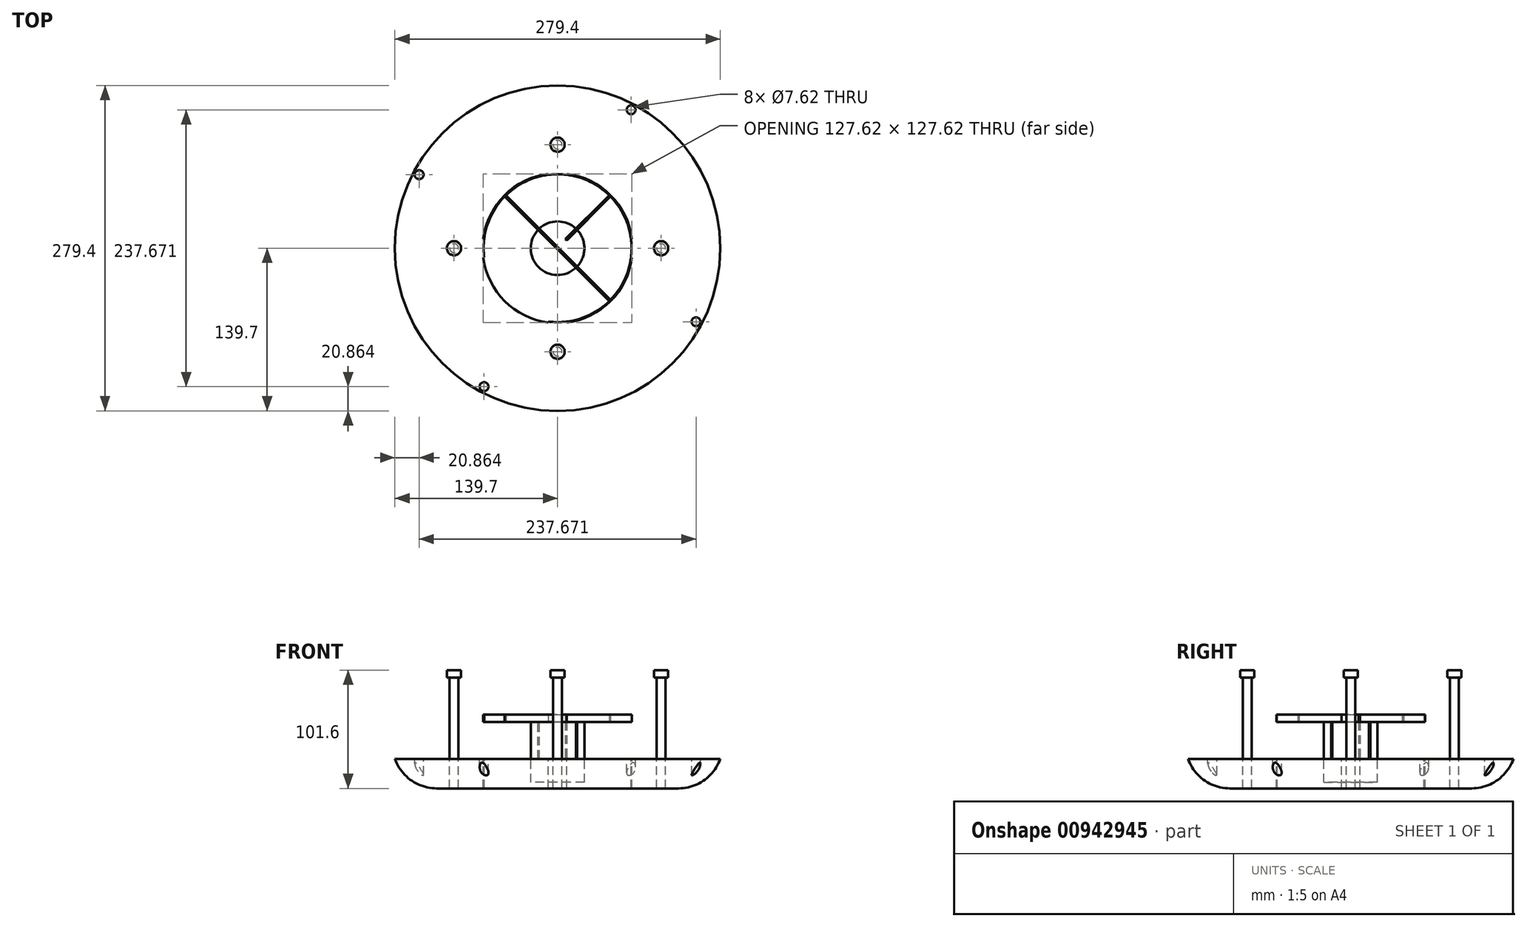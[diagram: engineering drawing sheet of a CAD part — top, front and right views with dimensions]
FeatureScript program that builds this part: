
annotation { "Feature Type Name" : "Feature", "Feature Type Description" : "" }
export const myFeature = defineFeature(function(context is Context, id is Id, definition is map)
    precondition{}
    {
        {
            var Q0;
            Q0=qCreatedBy(makeId("Top.planeOp"),FACE);
            var sketch = newSketch(context, id + "F0", { "sketchPlane" : qUnion([Q0])});
            skArc(sketch, "E0", {"start": v(-7.87, 63.01) * mm, "mid": v(-44.9, 44.9) * mm, "end": v(-63.01, 7.87) * mm});
            skArc(sketch, "E1", {"start": v(-7.87, 63.81) * mm, "mid": v(-45.46, 45.46) * mm, "end": v(-63.81, 7.87) * mm});
            skLineSegment(sketch, "E2", {"start": v(-7.87, 63.81) * mm, "end": v(-7.87, 63.01) * mm});
            skLineSegment(sketch, "E3", {"start": v(7.87, 63.01) * mm, "end": v(7.87, 63.81) * mm});
            skLineSegment(sketch, "E4.MirrorCS", {"start": v(-7.87, -63.81) * mm, "end": v(-7.87, -63.01) * mm});
            skLineSegment(sketch, "E5", {"start": v(-63.81, 7.87) * mm, "end": v(-63.01, 7.87) * mm});
            skLineSegment(sketch, "E6", {"start": v(-63.01, 7.87) * mm, "end": v(-63.81, 7.87) * mm});
            skLineSegment(sketch, "E7", {"start": v(63.01, 7.87) * mm, "end": v(63.81, 7.87) * mm});
            skLineSegment(sketch, "E8.MirrorCS", {"start": v(-63.81, -7.87) * mm, "end": v(-63.01, -7.87) * mm});
            skLineSegment(sketch, "E9.MirrorCS", {"start": v(63.01, -7.87) * mm, "end": v(63.81, -7.87) * mm});
            skLineSegment(sketch, "E10.MirrorCS", {"start": v(-63.01, -7.87) * mm, "end": v(-63.81, -7.87) * mm});
            skArc(sketch, "E11.trimOffspring", {"start": v(-63.81, -7.87) * mm, "mid": v(-45.46, -45.46) * mm, "end": v(-7.87, -63.81) * mm});
            skArc(sketch, "E12.trimOffspring", {"start": v(-63.01, -7.87) * mm, "mid": v(-44.9, -44.9) * mm, "end": v(-7.87, -63.01) * mm});
            skArc(sketch, "E13.trimOffspring", {"start": v(63.81, 7.87) * mm, "mid": v(45.46, 45.46) * mm, "end": v(7.87, 63.81) * mm});
            skArc(sketch, "E14.trimOffspring", {"start": v(63.01, 7.87) * mm, "mid": v(44.9, 44.9) * mm, "end": v(7.87, 63.01) * mm});
            skArc(sketch, "E15.trimOffspring", {"start": v(7.87, -63.01) * mm, "mid": v(44.9, -44.9) * mm, "end": v(63.01, -7.87) * mm});
            skArc(sketch, "E16.trimOffspring", {"start": v(7.87, -63.81) * mm, "mid": v(45.46, -45.46) * mm, "end": v(63.81, -7.87) * mm});
            skLineSegment(sketch, "E17", {"start": v(-9, 7.87) * mm, "end": v(44.34, -45.46) * mm});
            skLineSegment(sketch, "E18.MirrorCS", {"start": v(45.46, -44.34) * mm, "end": v(-44.34, 45.46) * mm});
            skLineSegment(sketch, "E19", {"start": v(44.34, -45.46) * mm, "end": v(-45.46, 44.34) * mm});
            skLineSegment(sketch, "E20", {"start": v(-7.87, -6.75) * mm, "end": v(-45.46, -44.34) * mm});
            skLineSegment(sketch, "E21", {"start": v(-45.46, -44.34) * mm, "end": v(-7.87, -6.75) * mm});
            skLineSegment(sketch, "E22.MirrorCS", {"start": v(-44.34, -45.46) * mm, "end": v(-6.75, -7.87) * mm});
            skLineSegment(sketch, "E23.trimOffspring", {"start": v(-7.87, 63.01) * mm, "end": v(-7.87, 63.81) * mm});
            skLineSegment(sketch, "E24.trimOffspring", {"start": v(-7.87, -63.01) * mm, "end": v(-7.87, -63.81) * mm});
            skLineSegment(sketch, "E25.trimOffspring", {"start": v(7.87, -63.01) * mm, "end": v(7.87, -63.81) * mm});
            skLineSegment(sketch, "E26.trimOffspring", {"start": v(6.75, 7.87) * mm, "end": v(44.34, 45.46) * mm});
            skLineSegment(sketch, "E27.trimOffspring", {"start": v(7.87, 6.75) * mm, "end": v(45.46, 44.34) * mm});
            skCircle(sketch, "E28", {"center": v(0, 0) * mm, "radius": 63.5 * mm});
            skCircle(sketch, "E29", {"center": v(0, 0) * mm, "radius": 139.7 * mm});
            skCircle(sketch, "E30", {"center": v(0, 0) * mm, "radius": 95.25 * mm});
            skLineSegment(sketch, "E31", {"start": v(-7.87, -6.75) * mm, "end": v(-6.75, -7.87) * mm});
            skLineSegment(sketch, "E32", {"start": v(6.75, 7.87) * mm, "end": v(7.87, 6.75) * mm});
            skPoint(sketch, "E33.orphan", {"position": v(-7.87, 7.87) * mm});
            skPoint(sketch, "E34.MirrorCS.start.orphan", {"position": v(-7.87, 0) * mm});
            skPoint(sketch, "E35.MirrorCS.start.orphan", {"position": v(7.87, 0) * mm});
            skLineSegment(sketch, "E36", {"start": v(-7.3, -7.3) * mm, "end": v(0, 0) * mm});
            skLineSegment(sketch, "E37", {"start": v(0, 63.5) * mm, "end": v(0, 88.9) * mm});
            skCircle(sketch, "E38", {"center": v(0, 88.9) * mm, "radius": 3.81 * mm});
            skCircle(sketch, "E39.MirrorC", {"center": v(0, -88.9) * mm, "radius": 3.81 * mm});
            skCircle(sketch, "E40.1.0", {"center": v(-88.9, 0) * mm, "radius": 3.81 * mm});
            skCircle(sketch, "E40.3.0", {"center": v(88.9, 0) * mm, "radius": 3.81 * mm});
            skLineSegment(sketch, "E41", {"start": v(68.85, 121.56) * mm, "end": v(63.11, 118.84) * mm});
            skCircle(sketch, "E42", {"center": v(63.11, 118.84) * mm, "radius": 3.81 * mm});
            skCircle(sketch, "E43.1.0", {"center": v(-118.84, 63.11) * mm, "radius": 3.81 * mm});
            skCircle(sketch, "E43.2.0", {"center": v(-63.11, -118.84) * mm, "radius": 3.81 * mm});
            skCircle(sketch, "E43.3.0", {"center": v(118.84, -63.11) * mm, "radius": 3.81 * mm});
            skSolve(sketch);
        }
        {
            var Q0;
            {var subQ4=sQuery(id+"F0.wireOp",EDGE,"E1");Q0=makeQuery(id+"F0.imprint","IMPRINT",FACE,{"disambiguationData":[TD([[makeQuery(id+"F0.imprint","IMPRINT",EDGE,{"derivedFrom":subQ4}),1.0]])]});}
            var Q1;
            {var subQ1=sQuery(id+"F0.wireOp",EDGE,"E10.MirrorCS");Q1=makeQuery(id+"F0.imprint","IMPRINT",FACE,{"disambiguationData":[TD([[makeQuery(id+"F0.imprint","IMPRINT",EDGE,{"derivedFrom":subQ1}),1.0]])]});}
            var Q2;
            {var subQ4=sQuery(id+"F0.wireOp",EDGE,"E13.trimOffspring");Q2=makeQuery(id+"F0.imprint","IMPRINT",FACE,{"disambiguationData":[TD([[makeQuery(id+"F0.imprint","IMPRINT",EDGE,{"derivedFrom":subQ4}),1.0]])]});}
            var Q3;
            {var subQ1=sQuery(id+"F0.wireOp",EDGE,"E16.trimOffspring");Q3=makeQuery(id+"F0.imprint","IMPRINT",FACE,{"disambiguationData":[TD([[makeQuery(id+"F0.imprint","IMPRINT",EDGE,{"derivedFrom":subQ1}),1.0]])]});}
            var Q4;
            {var subQ4=sQuery(id+"F0.wireOp",EDGE,"E28");var subQ6=sQuery(id+"F0.wireOp",EDGE,"E18.MirrorCS");var subQ7=makeQuery(id+"F0.imprint","INTERSECT",VERTEX,{"disambiguationData":[OD(0.0)],"derivedFrom":[subQ6,subQ4]});Q4=makeQuery(id+"F0.imprint","IMPRINT",FACE,{"disambiguationData":[TD([[makeQuery(id+"F0.imprint","IMPRINT",EDGE,{"disambiguationData":[TD([[subQ7,-1.0]])],"derivedFrom":subQ6}),1.0]])]});}
            var Q5;
            {var subQ0=sQuery(id+"F0.wireOp",EDGE,"E21");var subQ8=makeQuery(id+"F0.imprint","INTERSECT",VERTEX,{"derivedFrom":[sQuery(id+"F0.wireOp",EDGE,"E8.MirrorCS"),subQ0]});Q5=makeQuery(id+"F0.imprint","IMPRINT",FACE,{"disambiguationData":[TD([[makeQuery(id+"F0.imprint","IMPRINT",EDGE,{"disambiguationData":[TD([[subQ8,1.0]])],"derivedFrom":subQ0}),-1.0]])]});}
            var Q6;
            {var subQ4=sQuery(id+"F0.wireOp",EDGE,"E32");Q6=makeQuery(id+"F0.imprint","IMPRINT",FACE,{"disambiguationData":[TD([[makeQuery(id+"F0.imprint","IMPRINT",EDGE,{"derivedFrom":subQ4}),1.0]])]});}
            extrude(context, id + "F1", {"entities" : qUnion([Q0, Q1, Q2, Q3, Q4, Q5, Q6]), "depth" : 38.1 * mm, "offsetDistance" : 25.4 * mm});
        }
        {
            var Q0;
            {var subQ10=sQuery(id+"F0.wireOp",EDGE,"E1");Q0=makeQuery(id+"F0.imprint","IMPRINT",FACE,{"disambiguationData":[TD([[makeQuery(id+"F0.imprint","IMPRINT",EDGE,{"derivedFrom":subQ10}),-1.0]])]});}
            extrude(context, id + "F2", {"entities" : qUnion([Q0]), "oppositeDirection" : true, "depth" : 25.4 * mm, "offsetDistance" : 25.4 * mm});
        }
        {
            var Q0;
            Q0=makeQuery(id+"F0.imprint","IMPRINT",FACE,{"disambiguationData":[TD([[makeQuery(id+"F0.imprint","IMPRINT",EDGE,{"derivedFrom":sQuery(id+"F0.wireOp",EDGE,"E29")}),1.0]])]});
            extrude(context, id + "F3", {"entities" : qUnion([Q0]), "operationType" : NewBodyOperationType.ADD, "oppositeDirection" : true, "depth" : 25.4 * mm, "offsetDistance" : 25.4 * mm});
        }
        {
            var Q0;
            Q0=makeQuery(id+"F3.opExtrude","CAP_EDGE",EDGE,{"disambiguationData":[OSD([sQuery(id+"F0.wireOp",EDGE,"E29")])],"isStart":false});
            fillet(context, id + "F4", {"entities" : qUnion([Q0]), "radius" : 38.1 * mm, "tangentPropagation" : true, "allowEdgeOverflow" : false});
        }
        {
            var Q0;
            Q0=qCreatedBy(makeId("Top.planeOp"),FACE);
            var sketch = newSketch(context, id + "F5", { "sketchPlane" : qUnion([Q0])});
            skCircle(sketch, "E44", {"center": v(0, 0) * mm, "radius": 23 * mm});
            skSolve(sketch);
        }
        {
            var Q0;
            Q0=makeQuery(id+"F5.imprint","IMPRINT",FACE,{"disambiguationData":[TD([[makeQuery(id+"F5.imprint","IMPRINT",EDGE,{"derivedFrom":sQuery(id+"F5.wireOp",EDGE,"E44")}),1.0]])]});
            extrude(context, id + "F6", {"entities" : qUnion([Q0]), "oppositeDirection" : true, "depth" : 20.24 * mm, "offsetDistance" : 25.4 * mm});
        }
        {
            var Q0;
            Q0=makeQuery(id+"F5.imprint","IMPRINT",FACE,{"disambiguationData":[TD([[makeQuery(id+"F5.imprint","IMPRINT",EDGE,{"derivedFrom":sQuery(id+"F5.wireOp",EDGE,"E44")}),1.0]])]});
            var Q1;
            Q1=sQuery(id+"F5.wireOp",EDGE,"E44");
            extrude(context, id + "F7", {"entities" : qUnion([Q0]), "operationType" : NewBodyOperationType.ADD, "surfaceOperationType" : NewSurfaceOperationType.ADD, "surfaceEntities" : qUnion([Q1]), "depth" : 31.75 * mm, "offsetDistance" : 25.4 * mm});
        }
        {
            var Q0;
            Q0=makeQuery(id+"F0.imprint","IMPRINT",FACE,{"disambiguationData":[TD([[makeQuery(id+"F0.imprint","IMPRINT",EDGE,{"derivedFrom":sQuery(id+"F0.wireOp",EDGE,"E40.1.0")}),1.0]])]});
            extrude(context, id + "F8", {"entities" : qUnion([Q0]), "depth" : 69.85 * mm, "offsetDistance" : 25.4 * mm});
        }
        {
            var Q0;
            Q0=makeQuery(id+"F8.opExtrude","CAP_FACE",FACE,{"disambiguationData":[OSD([sQuery(id+"F0.wireOp",EDGE,"E40.1.0")])],"isStart":false});
            var sketch = newSketch(context, id + "F9", { "sketchPlane" : qUnion([Q0])});
            skCircle(sketch, "E45", {"center": v(-88.9, 0) * mm, "radius": 6.1 * mm});
            skPoint(sketch, "E46.center", {"position": v(0, 0) * mm});
            skSolve(sketch);
        }
        {
            var Q0;
            Q0=makeQuery(id+"F9.imprint","IMPRINT",FACE,{"disambiguationData":[TD([[makeQuery(id+"F9.imprint","IMPRINT",EDGE,{"derivedFrom":sQuery(id+"F9.wireOp",EDGE,"E45")}),1.0]])]});
            var Q1;
            Q1=makeQuery(id+"F9.imprint","IMPRINT",FACE,{"disambiguationData":[TD([[makeQuery(id+"F9.imprint","IMPRINT",EDGE,{"derivedFrom":makeQuery(id+"F8.opExtrude","CAP_EDGE",EDGE,{"disambiguationData":[OSD([sQuery(id+"F0.wireOp",EDGE,"E40.1.0")])],"isStart":false})}),1.0]])]});
            extrude(context, id + "F10", {"entities" : qUnion([Q0, Q1]), "operationType" : NewBodyOperationType.ADD, "depth" : 6.35 * mm, "offsetDistance" : 25.4 * mm});
        }
        {
            var Q0;
            Q0=qCreatedBy(makeId("Front.planeOp"),FACE);
            var sketch = newSketch(context, id + "F11", { "sketchPlane" : qUnion([Q0])});
            skLineSegment(sketch, "E47", {"start": v(0, 0) * mm, "end": v(0, 31.75) * mm});
            skSolve(sketch);
        }
        {
            var Q0;
            Q0=makeQuery(id+"F8.opExtrude","SWEPT_BODY",BODY,{"disambiguationData":[OSD([sQuery(id+"F0.wireOp",EDGE,"E40.1.0")])]});
            var Q1;
            Q1=sQuery(id+"F11.wireOp",EDGE,"E47");
            circularPattern(context, id + "F12", {"entities" : qUnion([Q0]), "axis" : qUnion([Q1]), "angle" : 360 * degree, "instanceCount" : 4, "equalSpace" : true});
        }
        {
            var Q0;
            {var subQ1=sQuery(id+"F0.wireOp",EDGE,"E21");Q0=makeQuery(id+"F0.imprint","IMPRINT",FACE,{"disambiguationData":[TD([[makeQuery(id+"F0.imprint","IMPRINT",EDGE,{"derivedFrom":subQ1}),-1.0]])]});}
            var Q1;
            {var subQ1=sQuery(id+"F0.wireOp",EDGE,"E10.MirrorCS");Q1=makeQuery(id+"F0.imprint","IMPRINT",FACE,{"disambiguationData":[TD([[makeQuery(id+"F0.imprint","IMPRINT",EDGE,{"derivedFrom":subQ1}),1.0]])]});}
            var Q2;
            {var subQ6=sQuery(id+"F0.wireOp",EDGE,"E18.MirrorCS");Q2=makeQuery(id+"F0.imprint","IMPRINT",FACE,{"disambiguationData":[TD([[makeQuery(id+"F0.imprint","IMPRINT",EDGE,{"derivedFrom":subQ6}),1.0]])]});}
            var Q3;
            Q3=makeQuery(id+"F0.imprint","IMPRINT",FACE,{"disambiguationData":[TD([[makeQuery(id+"F0.imprint","IMPRINT",EDGE,{"derivedFrom":sQuery(id+"F0.wireOp",EDGE,"E16.trimOffspring")}),1.0]])]});
            var Q4;
            Q4=makeQuery(id+"F0.imprint","IMPRINT",FACE,{"disambiguationData":[TD([[makeQuery(id+"F0.imprint","IMPRINT",EDGE,{"derivedFrom":sQuery(id+"F0.wireOp",EDGE,"E1")}),1.0]])]});
            var Q5;
            Q5=makeQuery(id+"F0.imprint","IMPRINT",FACE,{"disambiguationData":[TD([[makeQuery(id+"F0.imprint","IMPRINT",EDGE,{"derivedFrom":sQuery(id+"F0.wireOp",EDGE,"E13.trimOffspring")}),1.0]])]});
            var Q6;
            {var subQ0=sQuery(id+"F0.wireOp",EDGE,"E26.trimOffspring");Q6=makeQuery(id+"F0.imprint","IMPRINT",FACE,{"disambiguationData":[TD([[makeQuery(id+"F0.imprint","IMPRINT",EDGE,{"derivedFrom":subQ0}),-1.0]])]});}
            extrude(context, id + "F13", {"entities" : qUnion([Q0, Q1, Q2, Q3, Q4, Q5, Q6]), "operationType" : NewBodyOperationType.REMOVE, "depth" : 31.75 * mm, "offsetDistance" : 25.4 * mm});
        }
    });
